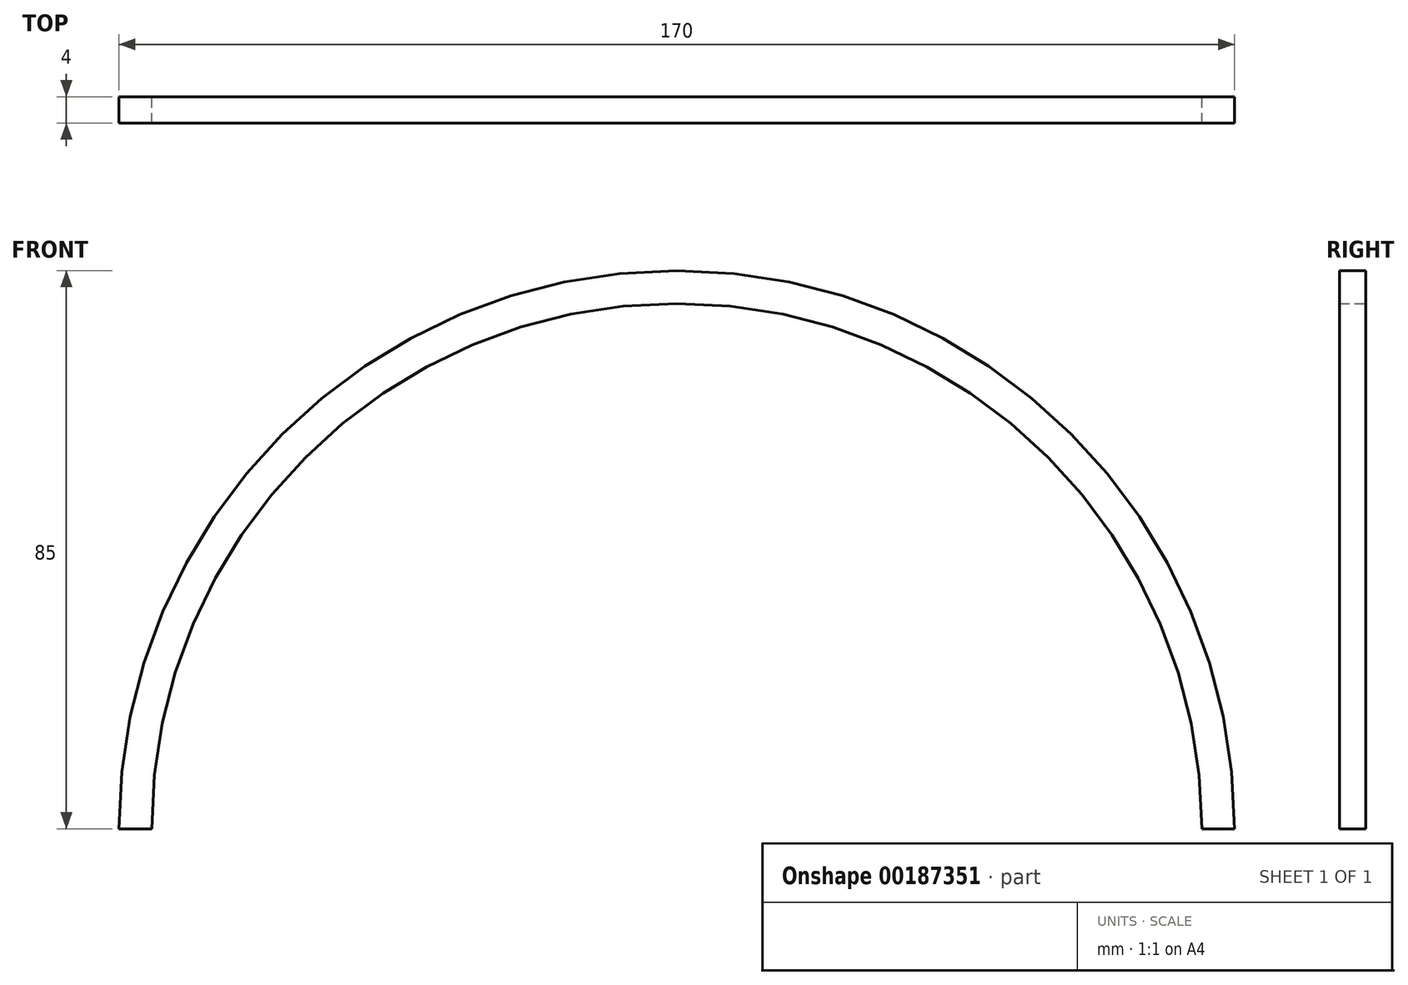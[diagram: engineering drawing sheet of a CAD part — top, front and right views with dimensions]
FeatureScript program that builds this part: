
annotation { "Feature Type Name" : "Feature", "Feature Type Description" : "" }
export const myFeature = defineFeature(function(context is Context, id is Id, definition is map)
    precondition{}
    {
        {
            var Q0;
            Q0=qCreatedBy(makeId("Front.planeOp"),FACE);
            var sketch = newSketch(context, id + "F0", { "sketchPlane" : qUnion([Q0])});
            skCircle(sketch, "E0", {"center": v(0, 0) * mm, "radius": 85 * mm});
            skCircle(sketch, "E1", {"center": v(0, 0) * mm, "radius": 80 * mm});
            skSolve(sketch);
        }
        {
            var Q0;
            Q0 = qSketchRegion(id + "F0", true);
            extrude(context, id + "F1", {"entities" : qUnion([Q0]), "depth" : 4 * mm});
        }
        {
            var Q0;
            Q0=makeQuery(id+"F1.opExtrude","CAP_FACE",FACE,{"disambiguationData":[OSD([sQuery(id+"F0.wireOp",EDGE,"E0"),sQuery(id+"F0.wireOp",EDGE,"E1")])],"isStart":false});
            var sketch = newSketch(context, id + "F2", { "sketchPlane" : qUnion([Q0])});
            skLineSegment(sketch, "E2.bottom", {"start": v(-93.37, 0) * mm, "end": v(110.62, 0) * mm});
            skLineSegment(sketch, "E2.top", {"start": v(-93.37, -98.25) * mm, "end": v(110.62, -98.25) * mm});
            skLineSegment(sketch, "E2.left", {"start": v(-93.37, 0) * mm, "end": v(-93.37, -98.25) * mm});
            skLineSegment(sketch, "E2.right", {"start": v(110.62, 0) * mm, "end": v(110.62, -98.25) * mm});
            skSolve(sketch);
        }
        {
            var Q0;
            Q0 = qSketchRegion(id + "F2", true);
            extrude(context, id + "F3", {"entities" : qUnion([Q0]), "operationType" : NewBodyOperationType.REMOVE, "oppositeDirection" : true, "depth" : 5 * mm});
        }
    });
